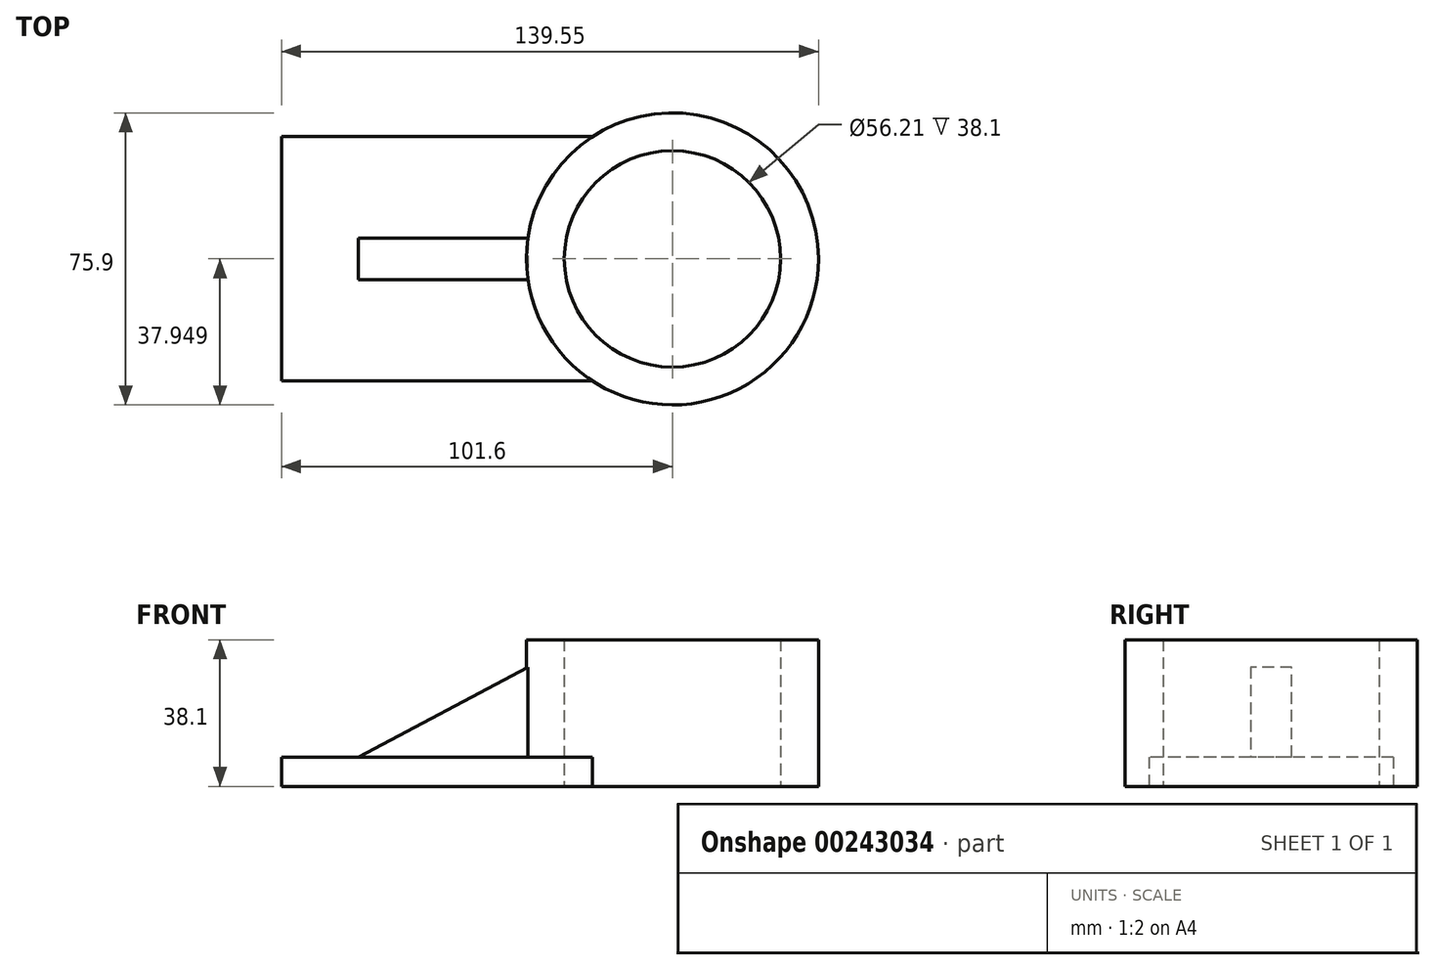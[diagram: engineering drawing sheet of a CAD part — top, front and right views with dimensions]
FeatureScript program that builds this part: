
annotation { "Feature Type Name" : "Feature", "Feature Type Description" : "" }
export const myFeature = defineFeature(function(context is Context, id is Id, definition is map)
    precondition{}
    {
        {
            var Q0;
            Q0=qCreatedBy(makeId("Top.planeOp"),FACE);
            var sketch = newSketch(context, id + "F0", { "sketchPlane" : qUnion([Q0])});
            skLineSegment(sketch, "E0.bottom", {"start": v(-51.39, 37.2) * mm, "end": v(29.43, 37.2) * mm});
            skLineSegment(sketch, "E0.top", {"start": v(-51.39, -26.3) * mm, "end": v(29.43, -26.3) * mm});
            skLineSegment(sketch, "E0.left", {"start": v(-51.39, 37.2) * mm, "end": v(-51.39, -26.3) * mm});
            skCircle(sketch, "E1", {"center": v(50.21, 5.45) * mm, "radius": 37.95 * mm});
            skCircle(sketch, "E2", {"center": v(50.21, 5.45) * mm, "radius": 28.1 * mm});
            skPoint(sketch, "E3.orphan", {"position": v(50.21, 37.2) * mm});
            skPoint(sketch, "E4.orphan", {"position": v(50.21, -26.3) * mm});
            skLineSegment(sketch, "E5.bottom", {"start": v(-31.35, 10.8) * mm, "end": v(12.64, 10.8) * mm});
            skLineSegment(sketch, "E5.top", {"start": v(-31.35, 0.1) * mm, "end": v(12.64, 0.1) * mm});
            skLineSegment(sketch, "E5.left", {"start": v(-31.35, 10.8) * mm, "end": v(-31.35, 0.1) * mm});
            skPoint(sketch, "E5.middle", {"position": v(12.26, 5.45) * mm});
            skPoint(sketch, "E5.right.end.orphan", {"position": v(55.88, 0.1) * mm});
            skPoint(sketch, "E5.right.start.orphan", {"position": v(55.88, 10.8) * mm});
            skSolve(sketch);
        }
        {
            var Q0;
            Q0=makeQuery(id+"F0.imprint","IMPRINT",FACE,{"disambiguationData":[TD([[makeQuery(id+"F0.imprint","IMPRINT",EDGE,{"derivedFrom":sQuery(id+"F0.wireOp",EDGE,"E2")}),-1.0]])]});
            extrude(context, id + "F1", {"entities" : qUnion([Q0]), "depth" : 38.1 * mm});
        }
        {
            var Q0;
            {var subQ1=sQuery(id+"F0.wireOp",EDGE,"E0.bottom");Q0=makeQuery(id+"F0.imprint","IMPRINT",FACE,{"disambiguationData":[TD([[makeQuery(id+"F0.imprint","IMPRINT",EDGE,{"derivedFrom":subQ1}),-1.0]])]});}
            extrude(context, id + "F2", {"entities" : qUnion([Q0]), "operationType" : NewBodyOperationType.ADD, "depth" : 7.62 * mm});
        }
        {
            var Q0;
            {var subQ0=sQuery(id+"F0.wireOp",EDGE,"E5.bottom");Q0=makeQuery(id+"F0.imprint","IMPRINT",FACE,{"disambiguationData":[TD([[makeQuery(id+"F0.imprint","IMPRINT",EDGE,{"derivedFrom":subQ0}),-1.0]])]});}
            extrude(context, id + "F3", {"entities" : qUnion([Q0]), "operationType" : NewBodyOperationType.ADD, "depth" : 30.99 * mm});
        }
        {
            var Q0;
            Q0=makeQuery(id+"F3.opExtrude","SWEPT_FACE",FACE,{"disambiguationData":[OSD([sQuery(id+"F0.wireOp",EDGE,"E5.top")])]});
            var sketch = newSketch(context, id + "F4", { "sketchPlane" : qUnion([Q0])});
            skLineSegment(sketch, "E6", {"start": v(12.64, 30.99) * mm, "end": v(-31.35, 7.62) * mm});
            skSolve(sketch);
        }
        {
            var Q0;
            Q0=makeQuery(id+"F4.imprint","IMPRINT",FACE,{"disambiguationData":[TD([[makeQuery(id+"F4.imprint","IMPRINT",EDGE,{"derivedFrom":sQuery(id+"F4.wireOp",EDGE,"E6")}),-1.0]])]});
            extrude(context, id + "F5", {"entities" : qUnion([Q0]), "operationType" : NewBodyOperationType.REMOVE, "oppositeDirection" : true, "depth" : 25.4 * mm});
        }
    });
